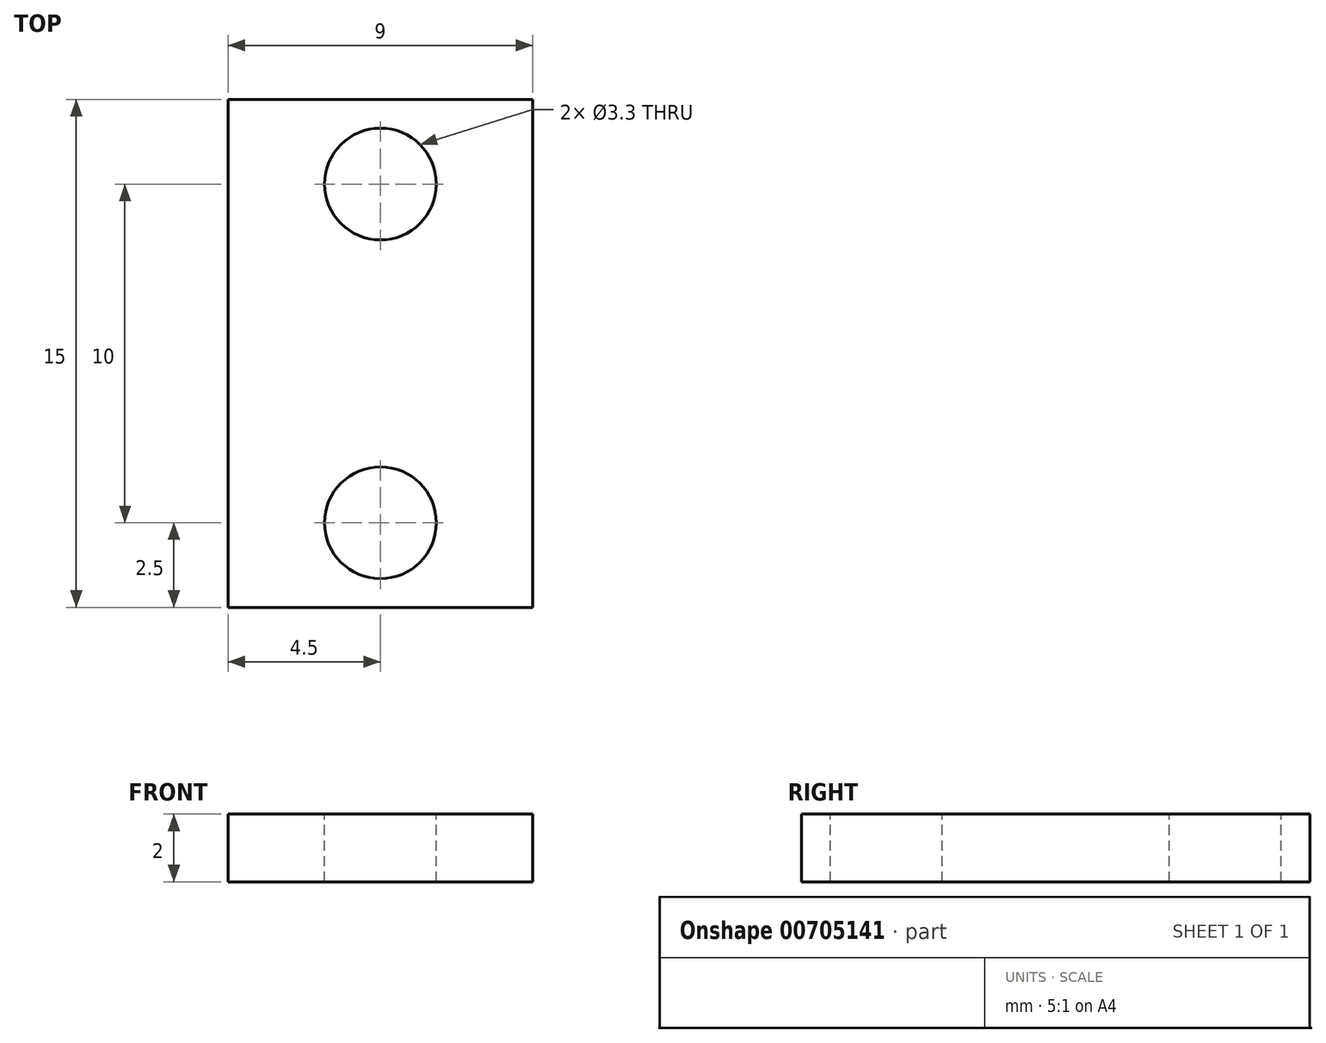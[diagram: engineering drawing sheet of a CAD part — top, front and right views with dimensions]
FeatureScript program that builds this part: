
annotation { "Feature Type Name" : "Feature", "Feature Type Description" : "" }
export const myFeature = defineFeature(function(context is Context, id is Id, definition is map)
    precondition{}
    {
        {
            var Q0;
            Q0=qCreatedBy(makeId("Top.planeOp"),FACE);
            var sketch = newSketch(context, id + "F0", { "sketchPlane" : qUnion([Q0])});
            skLineSegment(sketch, "E0.bottom", {"start": v(4.5, 7.5) * mm, "end": v(-4.5, 7.5) * mm});
            skLineSegment(sketch, "E0.top", {"start": v(4.5, -7.5) * mm, "end": v(-4.5, -7.5) * mm});
            skLineSegment(sketch, "E0.left", {"start": v(4.5, 7.5) * mm, "end": v(4.5, -7.5) * mm});
            skLineSegment(sketch, "E0.right", {"start": v(-4.5, 7.5) * mm, "end": v(-4.5, -7.5) * mm});
            skPoint(sketch, "E0.middle", {"position": v(0, 0) * mm});
            skSolve(sketch);
        }
        {
            var Q0;
            Q0 = qSketchRegion(id + "F0", true);
            extrude(context, id + "F1", {"entities" : qUnion([Q0]), "depth" : 2 * mm, "offsetDistance" : 25 * mm});
        }
        {
            var Q0;
            Q0=makeQuery(id+"F1.opExtrude","CAP_FACE",FACE,{"disambiguationData":[OSD([sQuery(id+"F0.wireOp",EDGE,"E0.bottom"),sQuery(id+"F0.wireOp",EDGE,"E0.top"),sQuery(id+"F0.wireOp",EDGE,"E0.left"),sQuery(id+"F0.wireOp",EDGE,"E0.right")])],"isStart":false});
            var sketch = newSketch(context, id + "F2", { "sketchPlane" : qUnion([Q0])});
            skLineSegment(sketch, "E1", {"start": v(-4.5, 0) * mm, "end": v(4.5, 0) * mm, "construction": true});
            skLineSegment(sketch, "E2", {"start": v(0, -7.5) * mm, "end": v(0, 7.5) * mm, "construction": true});
            skLineSegment(sketch, "E3", {"start": v(-4.5, 5) * mm, "end": v(4.5, 5) * mm, "construction": true});
            skCircle(sketch, "E4", {"center": v(0, 5) * mm, "radius": 1.55 * mm});
            skCircle(sketch, "E5.MirrorC", {"center": v(0, -5) * mm, "radius": 1.55 * mm});
            skLineSegment(sketch, "E6.MirrorCS", {"start": v(-4.5, -5) * mm, "end": v(4.5, -5) * mm, "construction": true});
            skSolve(sketch);
        }
        {
            var Q0;
            Q0=sQuery(id+"F2.wireOp",VERTEX,"E5.MirrorC.center");
            var Q1;
            Q1=sQuery(id+"F2.wireOp",VERTEX,"E4.center");
            var Q2;
            Q2=makeQuery(id+"F1.opExtrude","SWEPT_BODY",BODY,{"disambiguationData":[OSD([sQuery(id+"F0.wireOp",EDGE,"E0.bottom"),sQuery(id+"F0.wireOp",EDGE,"E0.top"),sQuery(id+"F0.wireOp",EDGE,"E0.left"),sQuery(id+"F0.wireOp",EDGE,"E0.right")])]});
            hole(context, id + "F3", {"style" : HoleStyle.SIMPLE, "endStyle" : HoleEndStyle.THROUGH, "standardTappedOrClearance" : lookupTablePath({ "standard" : "ISO", "fit" : "Normal", "size" : "M3", "type" : "Clearance" }), "standardBlindInLast" : lookupTablePath({ "fit" : "Standard", "standard" : "ISO", "size" : "M3", "type" : "Clearance" }), "holeDiameter" : 3.3 * mm, "majorDiameter" : 5 * mm, "isTappedThrough" : true, "tappedDepth" : 12 * mm, "tapClearance" : 3, "locations" : qUnion([Q0, Q1]), "scope" : qUnion([Q2])});
        }
    });
